# Revit family: 5in_Square_Xicato-M
name_source: partatom
category: Lighting Fixtures
revit_build: Autodesk Revit 2014 (Build: 20130308_1515(x64)
units: mm (PartAtom-declared; Revit-internal decimal feet)

## types (5) — shared parameters
Assembly Code = D5020210
Backbox = Hubbell-White
Color Filter = 16777215
Default Elevation = 48.000"
Description = Wide Distribution Directional Downlights
Dimming Lamp Color Temperature Shift = <None>
Emit Shape Visible in Rendering = No
Emit from Rectangle Length = 4.000"
Emit from Rectangle Width = 4.000"
Glass = Hubbell-White Glass
Lamp = LED Lamp
Load Classification = Lighting
Manufacturer = Kurt Versen
Model = 5in Square Xicato XTM Surface Forms-Wall Mount (M)
Power Factor = 1
Product Documentation Link = https://hubbellcdn.com
Product Page URL = https://www.hubbell.com
Tilt Angle = -90.00°
Type Comments = Lighting Fixture
URL = https://www.hubbell.com
Voltage = 120 V
Warranty = 5 Year Warranty
Wattage Comments = 12W,17W,24W

## per-type parameters (varying)
| type | Apparent Load | Beam Spread | Photometric Web File | Watts |
| L342_12W_Xicato_XTM_1100_lm_3000K | 12 VA | Wide | L342_12W_Xicato_XTM_1100_lm_3000K.IES | 12 W |
| L342_24W_Xicato_XTM_2100_lm_3000K | 24 VA | Wide | L342_24W_Xicato_XTM_2100_lm_3000K.IES | 24 W |
| L344_12W_Xicato_XTM_1100_lm_3000K | 12 VA | Medium | L344_12W_Xicato_XTM_1100_lm_3000K.IES | 12 W |
| L346_12W_Xicato_XTM_1100_lm_3000K | 12 VA | Narrow | L346_12W_Xicato_XTM_1100_lm_3000K.IES | 12 W |
| L346_24W_Xicato_XTM_2100_lm_3000K | 24 VA | Narrow | L346_24W_Xicato_XTM_2100_lm_3000K.IES | 24 W |

## geometry (parser evidence)
native form markers: Sweep x4
no freeform markers — native parametric forms only
